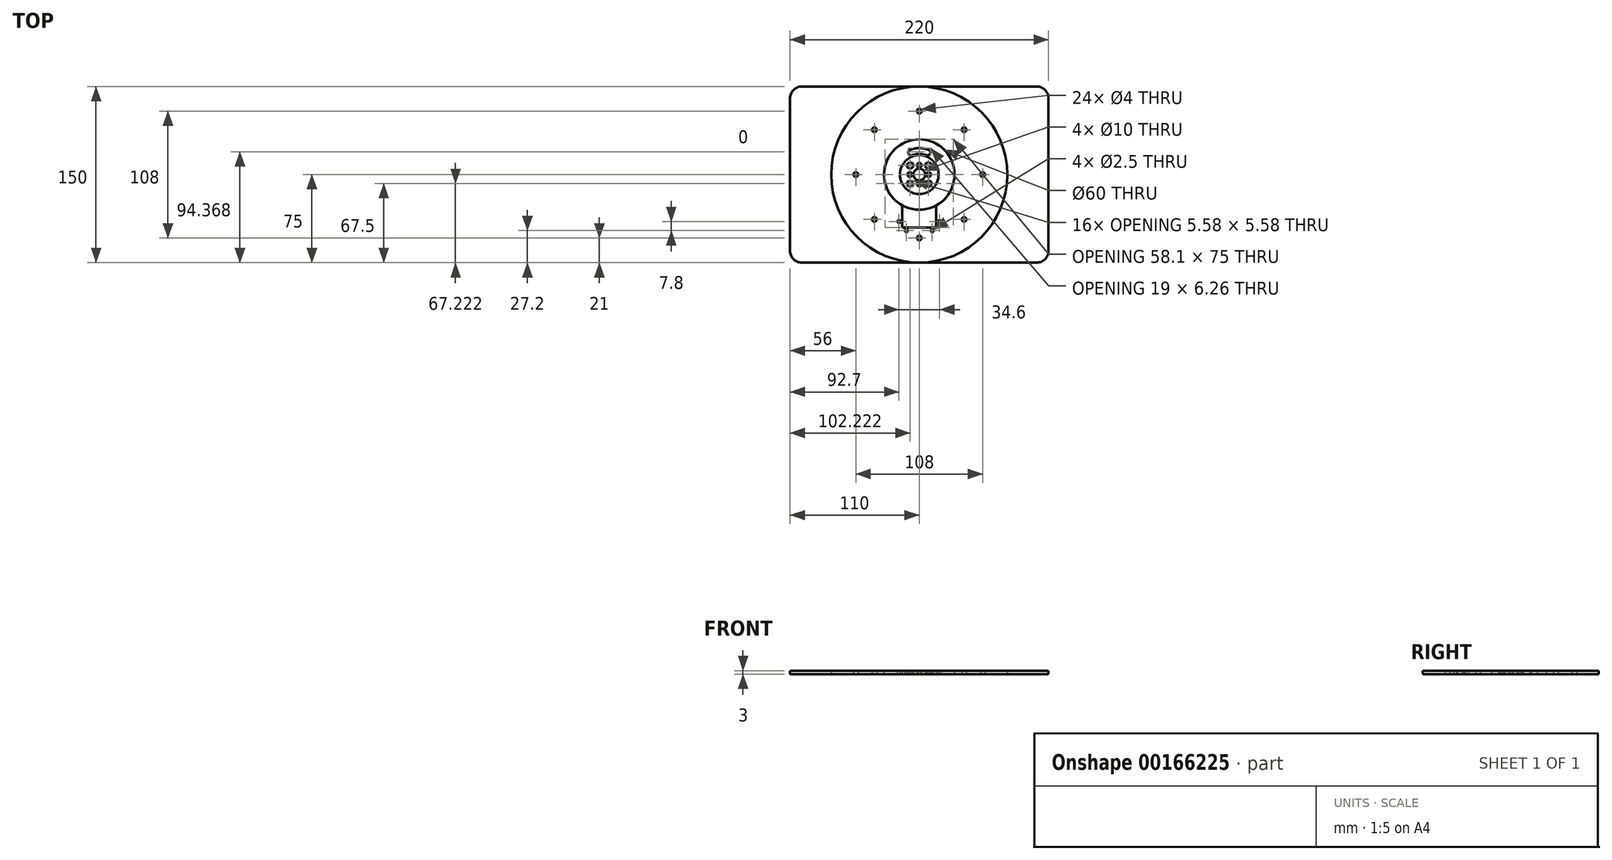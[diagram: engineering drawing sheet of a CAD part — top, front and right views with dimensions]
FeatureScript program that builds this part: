
annotation { "Feature Type Name" : "Feature", "Feature Type Description" : "" }
export const myFeature = defineFeature(function(context is Context, id is Id, definition is map)
    precondition{}
    {
        {
            var Q0;
            Q0=qCreatedBy(makeId("Top.planeOp"),FACE);
            var sketch = newSketch(context, id + "F0", { "sketchPlane" : qUnion([Q0])});
            skCircle(sketch, "E0", {"center": v(0, 0) * mm, "radius": 11 * mm, "construction": true});
            skCircle(sketch, "E1", {"center": v(0, 0) * mm, "radius": 5 * mm});
            skLineSegment(sketch, "E2", {"start": v(0, 0) * mm, "end": v(7.78, 7.78) * mm, "construction": true});
            skCircle(sketch, "E3", {"center": v(7.78, 7.78) * mm, "radius": 1.25 * mm});
            skCircle(sketch, "E4.1.0", {"center": v(-7.78, 7.78) * mm, "radius": 1.25 * mm});
            skCircle(sketch, "E4.2.0", {"center": v(-7.78, -7.78) * mm, "radius": 1.25 * mm});
            skCircle(sketch, "E4.3.0", {"center": v(7.78, -7.78) * mm, "radius": 1.25 * mm});
            skSolve(sketch);
        }
        {
            var Q0;
            Q0=qCreatedBy(makeId("Top.planeOp"),FACE);
            var sketch = newSketch(context, id + "F1", { "sketchPlane" : qUnion([Q0])});
            skCircle(sketch, "E5", {"center": v(0, 0) * mm, "radius": 11 * mm, "construction": true});
            skCircle(sketch, "E6", {"center": v(0, 0) * mm, "radius": 5 * mm});
            skLineSegment(sketch, "E7", {"start": v(0, 0) * mm, "end": v(7.78, 7.78) * mm, "construction": true});
            skCircle(sketch, "E8.cCircle", {"center": v(7.78, 7.78) * mm, "radius": 2.5 * mm, "construction": true});
            skLineSegment(sketch, "E8.0", {"start": v(9.82, 5.74) * mm, "end": v(7.03, 4.99) * mm});
            skLineSegment(sketch, "E8.1", {"start": v(7.03, 4.99) * mm, "end": v(4.99, 7.03) * mm});
            skLineSegment(sketch, "E8.2", {"start": v(4.99, 7.03) * mm, "end": v(5.74, 9.82) * mm});
            skLineSegment(sketch, "E8.3", {"start": v(5.74, 9.82) * mm, "end": v(8.53, 10.57) * mm});
            skLineSegment(sketch, "E8.4", {"start": v(8.53, 10.57) * mm, "end": v(10.57, 8.53) * mm});
            skLineSegment(sketch, "E8.5", {"start": v(10.57, 8.53) * mm, "end": v(9.82, 5.74) * mm});
            skPoint(sketch, "E8.0.midPoint", {"position": v(8.43, 5.36) * mm});
            skLineSegment(sketch, "E9.1.0", {"start": v(-4.99, 7.03) * mm, "end": v(-7.03, 4.99) * mm});
            skLineSegment(sketch, "E9.1.1", {"start": v(-7.03, 4.99) * mm, "end": v(-9.82, 5.74) * mm});
            skLineSegment(sketch, "E9.1.2", {"start": v(-9.82, 5.74) * mm, "end": v(-10.57, 8.53) * mm});
            skLineSegment(sketch, "E9.1.3", {"start": v(-10.57, 8.53) * mm, "end": v(-8.53, 10.57) * mm});
            skLineSegment(sketch, "E9.1.4", {"start": v(-8.53, 10.57) * mm, "end": v(-5.74, 9.82) * mm});
            skLineSegment(sketch, "E9.1.5", {"start": v(-5.74, 9.82) * mm, "end": v(-4.99, 7.03) * mm});
            skLineSegment(sketch, "E9.2.0", {"start": v(-7.03, -4.99) * mm, "end": v(-4.99, -7.03) * mm});
            skLineSegment(sketch, "E9.2.1", {"start": v(-4.99, -7.03) * mm, "end": v(-5.74, -9.82) * mm});
            skLineSegment(sketch, "E9.2.2", {"start": v(-5.74, -9.82) * mm, "end": v(-8.53, -10.57) * mm});
            skLineSegment(sketch, "E9.2.3", {"start": v(-8.53, -10.57) * mm, "end": v(-10.57, -8.53) * mm});
            skLineSegment(sketch, "E9.2.4", {"start": v(-10.57, -8.53) * mm, "end": v(-9.82, -5.74) * mm});
            skLineSegment(sketch, "E9.2.5", {"start": v(-9.82, -5.74) * mm, "end": v(-7.03, -4.99) * mm});
            skLineSegment(sketch, "E9.3.0", {"start": v(4.99, -7.03) * mm, "end": v(7.03, -4.99) * mm});
            skLineSegment(sketch, "E9.3.1", {"start": v(7.03, -4.99) * mm, "end": v(9.82, -5.74) * mm});
            skLineSegment(sketch, "E9.3.2", {"start": v(9.82, -5.74) * mm, "end": v(10.57, -8.53) * mm});
            skLineSegment(sketch, "E9.3.3", {"start": v(10.57, -8.53) * mm, "end": v(8.53, -10.57) * mm});
            skLineSegment(sketch, "E9.3.4", {"start": v(8.53, -10.57) * mm, "end": v(5.74, -9.82) * mm});
            skLineSegment(sketch, "E9.3.5", {"start": v(5.74, -9.82) * mm, "end": v(4.99, -7.03) * mm});
            skSolve(sketch);
        }
        {
            var Q0;
            Q0=qCreatedBy(makeId("Top.planeOp"),FACE);
            var sketch = newSketch(context, id + "F2", { "sketchPlane" : qUnion([Q0])});
            skLineSegment(sketch, "E10.bottom", {"start": v(-14.5, 14.5) * mm, "end": v(14.5, 14.5) * mm});
            skLineSegment(sketch, "E10.top", {"start": v(-14.5, -45) * mm, "end": v(14.5, -45) * mm});
            skLineSegment(sketch, "E10.left", {"start": v(-14.5, 14.5) * mm, "end": v(-14.5, -45) * mm});
            skLineSegment(sketch, "E10.right", {"start": v(14.5, 14.5) * mm, "end": v(14.5, -45) * mm});
            skCircle(sketch, "E11", {"center": v(17.3, 4) * mm, "radius": 1.25 * mm});
            skCircle(sketch, "E12.0.1.0", {"center": v(17.3, -18) * mm, "radius": 1.25 * mm});
            skCircle(sketch, "E12.0.2.0", {"center": v(17.3, -40) * mm, "radius": 1.25 * mm});
            skCircle(sketch, "E12.1.0.0", {"center": v(-17.3, 4) * mm, "radius": 1.25 * mm});
            skCircle(sketch, "E12.1.1.0", {"center": v(-17.3, -18) * mm, "radius": 1.25 * mm});
            skCircle(sketch, "E12.1.2.0", {"center": v(-17.3, -40) * mm, "radius": 1.25 * mm});
            skLineSegment(sketch, "E12.direction1", {"start": v(17.3, 4) * mm, "end": v(-17.3, 4) * mm, "construction": true});
            skLineSegment(sketch, "E12.direction2", {"start": v(17.3, 4) * mm, "end": v(17.3, -18) * mm, "construction": true});
            skCircle(sketch, "E13", {"center": v(11, -47.8) * mm, "radius": 1.25 * mm});
            skCircle(sketch, "E14.MirrorC", {"center": v(-11, -47.8) * mm, "radius": 1.25 * mm});
            skSolve(sketch);
        }
        {
            var Q0;
            Q0=qCreatedBy(makeId("Top.planeOp"),FACE);
            var sketch = newSketch(context, id + "F3", { "sketchPlane" : qUnion([Q0])});
            skCircle(sketch, "E15", {"center": v(0, 0) * mm, "radius": 75 * mm});
            skSolve(sketch);
        }
        {
            var Q0;
            Q0=qCreatedBy(makeId("Top.planeOp"),FACE);
            var sketch = newSketch(context, id + "F4", { "sketchPlane" : qUnion([Q0])});
            skLineSegment(sketch, "E16.bottom", {"start": v(-100, 75) * mm, "end": v(100, 75) * mm});
            skLineSegment(sketch, "E16.top", {"start": v(-100, -75) * mm, "end": v(100, -75) * mm});
            skLineSegment(sketch, "E16.left", {"start": v(-110, 65) * mm, "end": v(-110, -65) * mm});
            skLineSegment(sketch, "E16.right", {"start": v(110, 65) * mm, "end": v(110, -65) * mm});
            skPoint(sketch, "E17.visualSharp", {"position": v(-110, 75) * mm});
            skArc(sketch, "E17.filletArc", {"start": v(-100, 75) * mm, "mid": v(-107.07, 72.07) * mm, "end": v(-110, 65) * mm});
            skPoint(sketch, "E18.visualSharp", {"position": v(-110, -75) * mm});
            skArc(sketch, "E18.filletArc", {"start": v(-110, -65) * mm, "mid": v(-107.07, -72.07) * mm, "end": v(-100, -75) * mm});
            skPoint(sketch, "E19.visualSharp", {"position": v(110, -75) * mm});
            skArc(sketch, "E19.filletArc", {"start": v(100, -75) * mm, "mid": v(107.07, -72.07) * mm, "end": v(110, -65) * mm});
            skPoint(sketch, "E20.visualSharp", {"position": v(110, 75) * mm});
            skArc(sketch, "E20.filletArc", {"start": v(110, 65) * mm, "mid": v(107.07, 72.07) * mm, "end": v(100, 75) * mm});
            skSolve(sketch);
        }
        {
            var Q0;
            Q0=qCreatedBy(makeId("Top.planeOp"),FACE);
            var sketch = newSketch(context, id + "F5", { "sketchPlane" : qUnion([Q0])});
            skCircle(sketch, "E21", {"center": v(0, 0) * mm, "radius": 54 * mm, "construction": true});
            skCircle(sketch, "E22", {"center": v(0, 54) * mm, "radius": 2 * mm});
            skCircle(sketch, "E23.1.0", {"center": v(-54, 0) * mm, "radius": 2 * mm});
            skCircle(sketch, "E23.2.0", {"center": v(0, -54) * mm, "radius": 2 * mm});
            skCircle(sketch, "E23.3.0", {"center": v(54, 0) * mm, "radius": 2 * mm});
            skSolve(sketch);
        }
        {
            var Q0;
            Q0=qCreatedBy(makeId("Top.planeOp"),FACE);
            var sketch = newSketch(context, id + "F6", { "sketchPlane" : qUnion([Q0])});
            skPoint(sketch, "E24.center", {"position": v(0, 0) * mm});
            skCircle(sketch, "E25", {"center": v(0, 0) * mm, "radius": 54 * mm, "construction": true});
            skCircle(sketch, "E26", {"center": v(38.18, 38.18) * mm, "radius": 2 * mm});
            skLineSegment(sketch, "E27", {"start": v(38.18, 38.18) * mm, "end": v(38.18, 0) * mm, "construction": true});
            skLineSegment(sketch, "E28", {"start": v(38.18, 0) * mm, "end": v(38.18, 38.18) * mm, "construction": true});
            skLineSegment(sketch, "E29", {"start": v(0, 38.18) * mm, "end": v(38.18, 38.18) * mm, "construction": true});
            skCircle(sketch, "E30.1.0", {"center": v(-38.18, 38.18) * mm, "radius": 2 * mm});
            skCircle(sketch, "E30.2.0", {"center": v(-38.18, -38.18) * mm, "radius": 2 * mm});
            skCircle(sketch, "E30.3.0", {"center": v(38.18, -38.18) * mm, "radius": 2 * mm});
            skSolve(sketch);
        }
        {
            var Q0;
            Q0=qCreatedBy(makeId("Top.planeOp"),FACE);
            var sketch = newSketch(context, id + "F7", { "sketchPlane" : qUnion([Q0])});
            skCircle(sketch, "E31", {"center": v(0, 0) * mm, "radius": 30 * mm});
            skSolve(sketch);
        }
        {
            var Q0;
            Q0=qCreatedBy(makeId("Top.planeOp"),FACE);
            var sketch = newSketch(context, id + "F8", { "sketchPlane" : qUnion([Q0])});
            skArc(sketch, "E32", {"start": v(-7, 18.73) * mm, "mid": v(0, 20) * mm, "end": v(7, 18.73) * mm});
            skArc(sketch, "E33.0.startCap", {"start": v(-6.13, 16.4) * mm, "mid": v(-9.34, 17.86) * mm, "end": v(-7.88, 21.08) * mm});
            skArc(sketch, "E33.0.endCap", {"start": v(7.88, 21.08) * mm, "mid": v(9.34, 17.86) * mm, "end": v(6.13, 16.4) * mm});
            skArc(sketch, "E33.0.left", {"start": v(-7.88, 21.08) * mm, "mid": v(0, 22.5) * mm, "end": v(7.88, 21.08) * mm});
            skArc(sketch, "E33.0.right", {"start": v(-6.13, 16.4) * mm, "mid": v(0, 17.5) * mm, "end": v(6.12, 16.4) * mm});
            skSolve(sketch);
        }
        {
            var Q0;
            Q0=qCreatedBy(makeId("Top.planeOp"),FACE);
            var sketch = newSketch(context, id + "F9", { "sketchPlane" : qUnion([Q0])});
            skCircle(sketch, "E34", {"center": v(0, 0) * mm, "radius": 16.5 * mm});
            skSolve(sketch);
        }
        {
            var Q0;
            Q0=qCreatedBy(makeId("Top.planeOp"),FACE);
            var sketch = newSketch(context, id + "F10", { "sketchPlane" : qUnion([Q0])});
            skCircle(sketch, "E35", {"center": v(0, 0) * mm, "radius": 8 * mm, "construction": true});
            skCircle(sketch, "E36", {"center": v(0, 8) * mm, "radius": 2 * mm});
            skCircle(sketch, "E37.1.0", {"center": v(-8, 0) * mm, "radius": 2 * mm});
            skCircle(sketch, "E37.2.0", {"center": v(0, -8) * mm, "radius": 2 * mm});
            skCircle(sketch, "E37.3.0", {"center": v(8, 0) * mm, "radius": 2 * mm});
            skSolve(sketch);
        }
        {
            var Q0;
            Q0=qCreatedBy(makeId("Top.planeOp"),FACE);
            var sketch = newSketch(context, id + "F11", { "sketchPlane" : qUnion([Q0])});
            skCircle(sketch, "E38", {"center": v(0, 0) * mm, "radius": 8 * mm, "construction": true});
            skCircle(sketch, "E39", {"center": v(0, 8) * mm, "radius": 1 * mm});
            skCircle(sketch, "E40.1.0", {"center": v(-8, 0) * mm, "radius": 1 * mm});
            skCircle(sketch, "E40.2.0", {"center": v(0, -8) * mm, "radius": 1 * mm});
            skCircle(sketch, "E40.3.0", {"center": v(8, 0) * mm, "radius": 1 * mm});
            skSolve(sketch);
        }
        {
            var Q0;
            Q0 = qSketchRegion(id + "F4", true);
            extrude(context, id + "F12", {"entities" : qUnion([Q0]), "depth" : 3 * mm});
        }
        {
            var Q0;
            Q0 = qSketchRegion(id + "F2", true);
            var Q1;
            Q1 = qSketchRegion(id + "F6", true);
            var Q2;
            Q2 = qSketchRegion(id + "F8", true);
            extrude(context, id + "F13", {"entities" : qUnion([Q0, Q1, Q2]), "operationType" : NewBodyOperationType.REMOVE, "depth" : 25 * mm});
        }
        {
            var Q0;
            Q0=makeQuery(id+"F3.imprint","IMPRINT",FACE,{"disambiguationData":[TD([[makeQuery(id+"F3.imprint","IMPRINT",EDGE,{"derivedFrom":sQuery(id+"F3.wireOp",EDGE,"E15")}),1.0]])]});
            extrude(context, id + "F14", {"entities" : qUnion([Q0]), "depth" : 3 * mm});
        }
        {
            var Q0;
            Q0 = qSketchRegion(id + "F5", true);
            var Q1;
            Q1 = qSketchRegion(id + "F7", true);
            extrude(context, id + "F15", {"entities" : qUnion([Q0, Q1]), "operationType" : NewBodyOperationType.REMOVE, "depth" : 25 * mm});
        }
        {
            var Q0;
            Q0=makeQuery(id+"F3.imprint","IMPRINT",FACE,{"disambiguationData":[TD([[makeQuery(id+"F3.imprint","IMPRINT",EDGE,{"derivedFrom":sQuery(id+"F3.wireOp",EDGE,"E15")}),1.0]])]});
            extrude(context, id + "F16", {"entities" : qUnion([Q0]), "depth" : 3 * mm});
        }
        {
            var Q0;
            Q0 = qSketchRegion(id + "F0", true);
            var Q1;
            Q1 = qSketchRegion(id + "F8", true);
            extrude(context, id + "F17", {"entities" : qUnion([Q0, Q1]), "operationType" : NewBodyOperationType.REMOVE, "depth" : 25 * mm});
        }
        {
            var Q0;
            Q0 = qSketchRegion(id + "F9", true);
            extrude(context, id + "F18", {"entities" : qUnion([Q0]), "depth" : 3 * mm});
        }
        {
            var Q0;
            Q0 = qSketchRegion(id + "F0", true);
            var Q1;
            Q1 = qSketchRegion(id + "F11", true);
            extrude(context, id + "F19", {"entities" : qUnion([Q0, Q1]), "operationType" : NewBodyOperationType.REMOVE, "depth" : 25 * mm});
        }
        {
            var Q0;
            Q0 = qSketchRegion(id + "F9", true);
            extrude(context, id + "F20", {"entities" : qUnion([Q0]), "depth" : 3 * mm});
        }
        {
            var Q0;
            Q0 = qSketchRegion(id + "F0", true);
            var Q1;
            Q1 = qSketchRegion(id + "F10", true);
            extrude(context, id + "F21", {"entities" : qUnion([Q0, Q1]), "operationType" : NewBodyOperationType.REMOVE, "depth" : 25 * mm});
        }
        {
            var Q0;
            Q0 = qSketchRegion(id + "F9", true);
            extrude(context, id + "F22", {"entities" : qUnion([Q0]), "depth" : 3 * mm});
        }
        {
            var Q0;
            Q0 = qSketchRegion(id + "F11", true);
            var Q1;
            Q1 = qSketchRegion(id + "F1", true);
            extrude(context, id + "F23", {"entities" : qUnion([Q0, Q1]), "operationType" : NewBodyOperationType.REMOVE, "depth" : 25 * mm});
        }
    });
